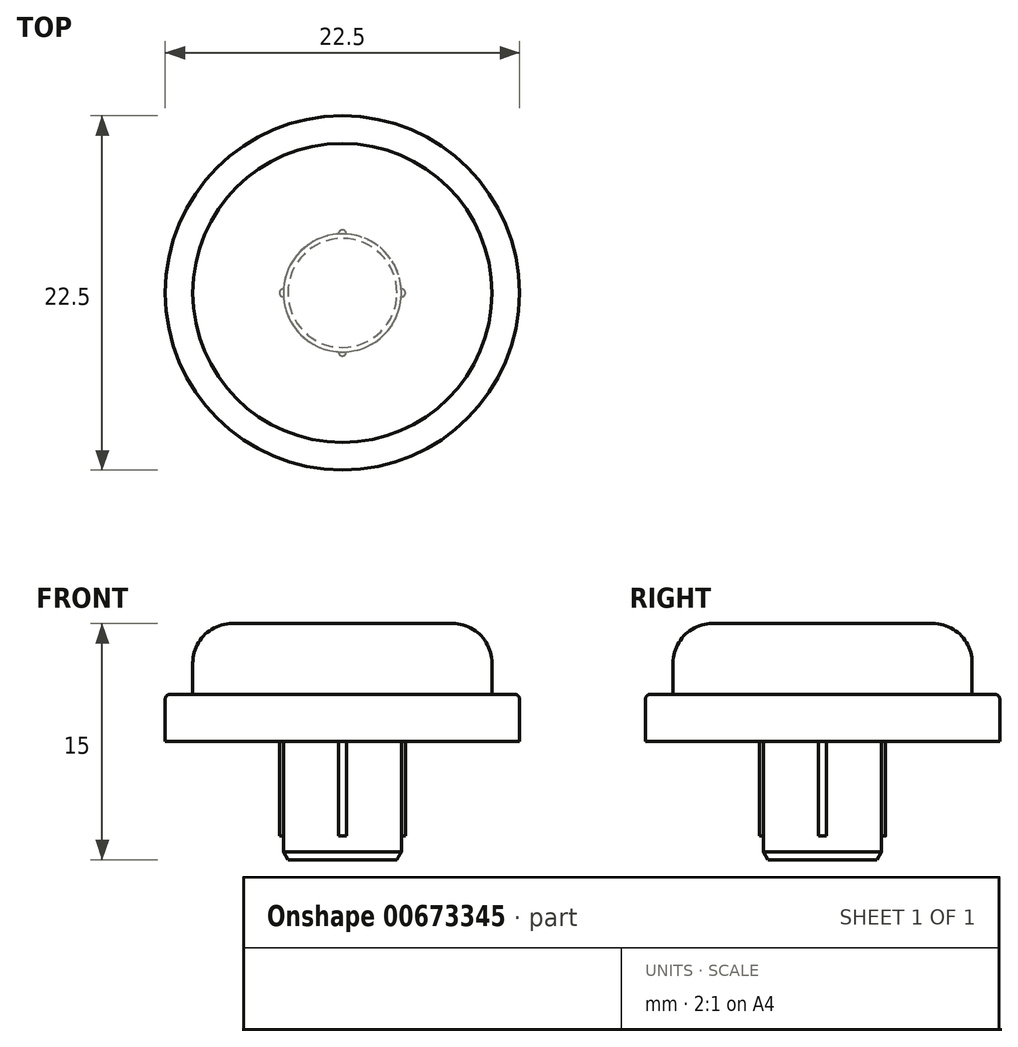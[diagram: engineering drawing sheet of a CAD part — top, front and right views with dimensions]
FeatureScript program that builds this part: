
annotation { "Feature Type Name" : "Feature", "Feature Type Description" : "" }
export const myFeature = defineFeature(function(context is Context, id is Id, definition is map)
    precondition{}
    {
        {
            var Q0;
            Q0=qCreatedBy(makeId("Top.planeOp"),FACE);
            var sketch = newSketch(context, id + "F0", { "sketchPlane" : qUnion([Q0])});
            skCircle(sketch, "E0", {"center": v(0, 0) * mm, "radius": 11.25 * mm});
            skSolve(sketch);
        }
        {
            var Q0;
            Q0=makeQuery(id+"F0.imprint","IMPRINT",FACE,{"disambiguationData":[TD([[makeQuery(id+"F0.imprint","IMPRINT",EDGE,{"derivedFrom":sQuery(id+"F0.wireOp",EDGE,"E0")}),1.0]])]});
            extrude(context, id + "F1", {"entities" : qUnion([Q0]), "depth" : 3 * mm, "offsetDistance" : 25 * mm});
        }
        {
            var Q0;
            Q0=qCreatedBy(makeId("Top.planeOp"),FACE);
            var sketch = newSketch(context, id + "F2", { "sketchPlane" : qUnion([Q0])});
            skCircle(sketch, "E1", {"center": v(0, 0) * mm, "radius": 9.5 * mm});
            skSolve(sketch);
        }
        {
            var Q0;
            Q0=makeQuery(id+"F2.imprint","IMPRINT",FACE,{"disambiguationData":[TD([[makeQuery(id+"F2.imprint","IMPRINT",EDGE,{"derivedFrom":sQuery(id+"F2.wireOp",EDGE,"E1")}),1.0]])]});
            extrude(context, id + "F3", {"entities" : qUnion([Q0]), "operationType" : NewBodyOperationType.ADD, "depth" : 7.5 * mm, "offsetDistance" : 25 * mm});
        }
        {
            var Q0;
            Q0=qCreatedBy(makeId("Top.planeOp"),FACE);
            var sketch = newSketch(context, id + "F4", { "sketchPlane" : qUnion([Q0])});
            skCircle(sketch, "E2", {"center": v(0, 0) * mm, "radius": 3.75 * mm});
            skSolve(sketch);
        }
        {
            var Q0;
            Q0=makeQuery(id+"F4.imprint","IMPRINT",FACE,{"disambiguationData":[TD([[makeQuery(id+"F4.imprint","IMPRINT",EDGE,{"derivedFrom":sQuery(id+"F4.wireOp",EDGE,"E2")}),1.0]])]});
            extrude(context, id + "F5", {"entities" : qUnion([Q0]), "operationType" : NewBodyOperationType.ADD, "oppositeDirection" : true, "depth" : 7.5 * mm, "offsetDistance" : 25 * mm});
        }
        {
            var Q0;
            Q0=qCreatedBy(makeId("Top.planeOp"),FACE);
            var sketch = newSketch(context, id + "F6", { "sketchPlane" : qUnion([Q0])});
            skCircle(sketch, "E3", {"center": v(-3.75, 0) * mm, "radius": 0.25 * mm});
            skCircle(sketch, "E4", {"center": v(3.75, 0) * mm, "radius": 0.25 * mm});
            skCircle(sketch, "E5", {"center": v(0, 3.75) * mm, "radius": 0.25 * mm});
            skCircle(sketch, "E6", {"center": v(0, -3.75) * mm, "radius": 0.25 * mm});
            skSolve(sketch);
        }
        {
            var Q0;
            Q0=makeQuery(id+"F6.imprint","IMPRINT",FACE,{"disambiguationData":[TD([[makeQuery(id+"F6.imprint","IMPRINT",EDGE,{"derivedFrom":sQuery(id+"F6.wireOp",EDGE,"E5")}),1.0]])]});
            var Q1;
            Q1=makeQuery(id+"F6.imprint","IMPRINT",FACE,{"disambiguationData":[TD([[makeQuery(id+"F6.imprint","IMPRINT",EDGE,{"derivedFrom":sQuery(id+"F6.wireOp",EDGE,"E4")}),1.0]])]});
            var Q2;
            Q2=makeQuery(id+"F6.imprint","IMPRINT",FACE,{"disambiguationData":[TD([[makeQuery(id+"F6.imprint","IMPRINT",EDGE,{"derivedFrom":sQuery(id+"F6.wireOp",EDGE,"E6")}),1.0]])]});
            var Q3;
            Q3=makeQuery(id+"F6.imprint","IMPRINT",FACE,{"disambiguationData":[TD([[makeQuery(id+"F6.imprint","IMPRINT",EDGE,{"derivedFrom":sQuery(id+"F6.wireOp",EDGE,"E3")}),1.0]])]});
            extrude(context, id + "F7", {"entities" : qUnion([Q0, Q1, Q2, Q3]), "operationType" : NewBodyOperationType.ADD, "oppositeDirection" : true, "depth" : 6 * mm, "offsetDistance" : 25 * mm});
        }
        {
            var Q0;
            Q0=makeQuery(id+"F5.opExtrude","CAP_EDGE",EDGE,{"disambiguationData":[OSD([sQuery(id+"F4.wireOp",EDGE,"E2")])],"isStart":false});
            chamfer(context, id + "F8", {"entities" : qUnion([Q0]), "chamferType" : ChamferType.OFFSET_ANGLE, "width" : 0.5 * mm, "oppositeDirection" : false, "angle" : 30 * degree, "tangentPropagation" : true});
        }
        {
            var Q0;
            Q0=makeQuery(id+"F1.opExtrude","CAP_EDGE",EDGE,{"disambiguationData":[OSD([sQuery(id+"F0.wireOp",EDGE,"E0")])],"isStart":false});
            fillet(context, id + "F9", {"entities" : qUnion([Q0]), "radius" : 0.3 * mm, "tangentPropagation" : true, "allowEdgeOverflow" : false});
        }
        {
            var Q0;
            Q0=makeQuery(id+"F3.opExtrude","CAP_EDGE",EDGE,{"disambiguationData":[OSD([sQuery(id+"F2.wireOp",EDGE,"E1")])],"isStart":false});
            fillet(context, id + "F10", {"entities" : qUnion([Q0]), "radius" : 2.5 * mm, "tangentPropagation" : true, "allowEdgeOverflow" : false});
        }
    });
